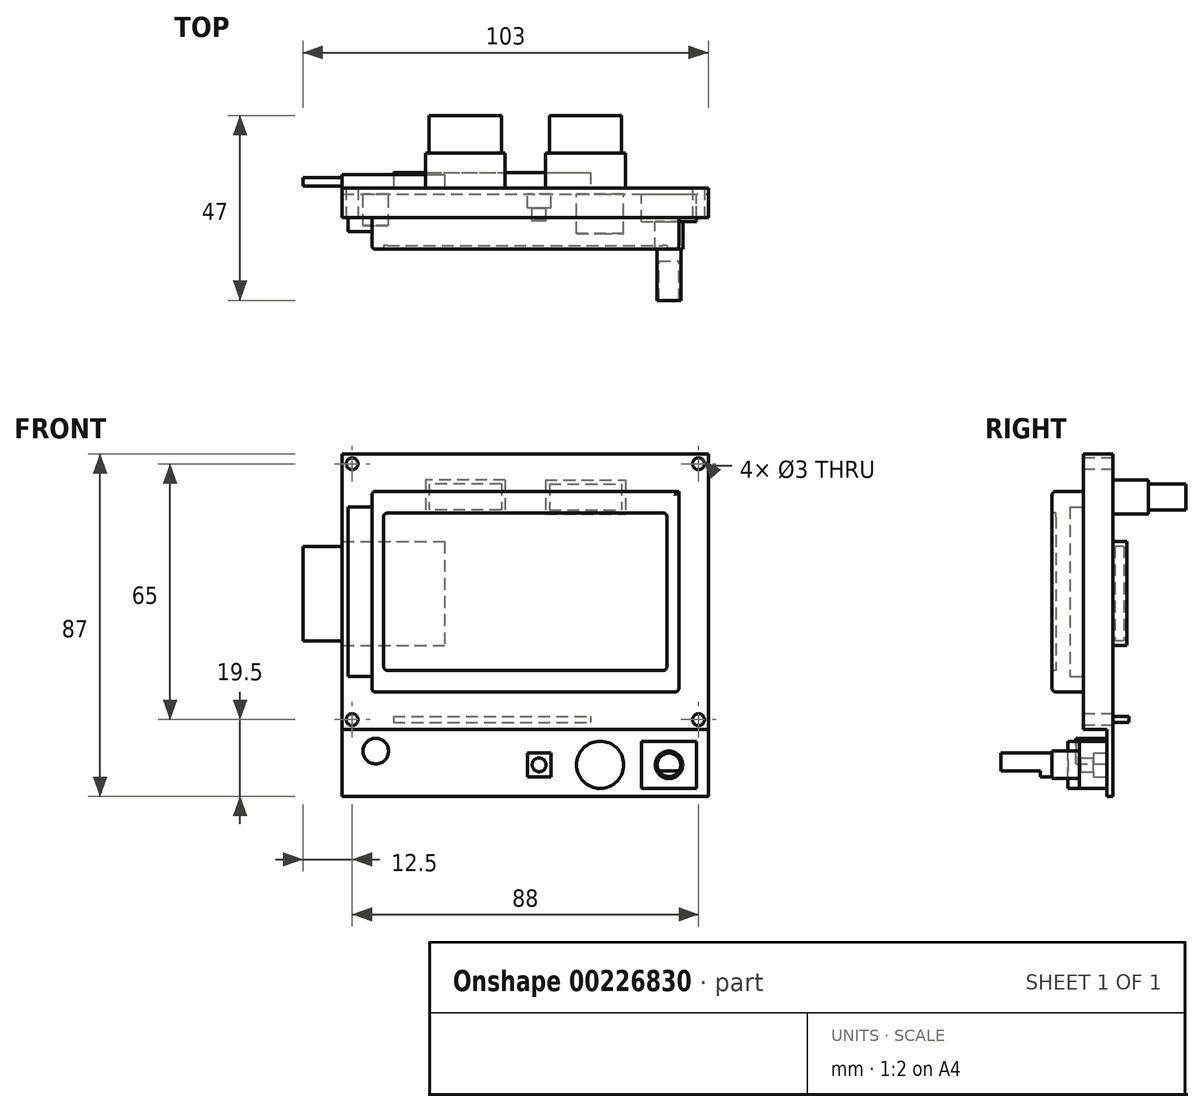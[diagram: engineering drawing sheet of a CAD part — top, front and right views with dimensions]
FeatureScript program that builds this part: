
annotation { "Feature Type Name" : "Feature", "Feature Type Description" : "" }
export const myFeature = defineFeature(function(context is Context, id is Id, definition is map)
    precondition{}
    {
        {
            var Q0;
            Q0=qCreatedBy(makeId("Front.planeOp"),FACE);
            var sketch = newSketch(context, id + "F0", { "sketchPlane" : qUnion([Q0])});
            skLineSegment(sketch, "E0.bottom", {"start": v(0, 0) * mm, "end": v(93, 0) * mm});
            skLineSegment(sketch, "E0.top", {"start": v(0, 87) * mm, "end": v(93, 87) * mm});
            skLineSegment(sketch, "E0.left", {"start": v(0, 0) * mm, "end": v(0, 87) * mm});
            skLineSegment(sketch, "E0.right", {"start": v(93, 0) * mm, "end": v(93, 87) * mm});
            skLineSegment(sketch, "E1", {"start": v(0, 17) * mm, "end": v(93, 17) * mm});
            skLineSegment(sketch, "E2.bottom", {"start": v(2.5, 84.5) * mm, "end": v(90.5, 84.5) * mm, "construction": true});
            skLineSegment(sketch, "E2.top", {"start": v(2.5, 19.5) * mm, "end": v(90.5, 19.5) * mm, "construction": true});
            skLineSegment(sketch, "E2.left", {"start": v(2.5, 84.5) * mm, "end": v(2.5, 19.5) * mm, "construction": true});
            skLineSegment(sketch, "E2.right", {"start": v(90.5, 84.5) * mm, "end": v(90.5, 19.5) * mm, "construction": true});
            skCircle(sketch, "E3", {"center": v(2.5, 84.5) * mm, "radius": 1.5 * mm});
            skCircle(sketch, "E4", {"center": v(90.5, 84.5) * mm, "radius": 1.5 * mm});
            skCircle(sketch, "E5", {"center": v(2.5, 19.5) * mm, "radius": 1.5 * mm});
            skCircle(sketch, "E6", {"center": v(90.5, 19.5) * mm, "radius": 1.5 * mm});
            skLineSegment(sketch, "E7", {"start": v(0, 8) * mm, "end": v(93, 8) * mm, "construction": true});
            skLineSegment(sketch, "E8", {"start": v(83, 11.72) * mm, "end": v(83, 4.4) * mm, "construction": true});
            skLineSegment(sketch, "E9.bottom", {"start": v(76, 2) * mm, "end": v(90, 2) * mm});
            skLineSegment(sketch, "E9.top", {"start": v(76, 14) * mm, "end": v(90, 14) * mm});
            skLineSegment(sketch, "E9.left", {"start": v(76, 2) * mm, "end": v(76, 14) * mm});
            skLineSegment(sketch, "E9.right", {"start": v(90, 2) * mm, "end": v(90, 14) * mm});
            skPoint(sketch, "E9.middle", {"position": v(83, 8) * mm});
            skCircle(sketch, "E10", {"center": v(83, 8) * mm, "radius": 3.5 * mm});
            skCircle(sketch, "E11", {"center": v(83, 8) * mm, "radius": 3 * mm});
            skLineSegment(sketch, "E12", {"start": v(80.4, 6.5) * mm, "end": v(85.6, 6.5) * mm});
            skCircle(sketch, "E13", {"center": v(65.5, 8) * mm, "radius": 6 * mm});
            skLineSegment(sketch, "E14.bottom", {"start": v(53, 11) * mm, "end": v(47, 11) * mm});
            skLineSegment(sketch, "E14.top", {"start": v(53, 5) * mm, "end": v(47, 5) * mm});
            skLineSegment(sketch, "E14.left", {"start": v(53, 11) * mm, "end": v(53, 5) * mm});
            skLineSegment(sketch, "E14.right", {"start": v(47, 11) * mm, "end": v(47, 5) * mm});
            skPoint(sketch, "E14.middle", {"position": v(50, 8) * mm});
            skCircle(sketch, "E15", {"center": v(50, 8) * mm, "radius": 1.75 * mm});
            skLineSegment(sketch, "E16", {"start": v(0, 11.5) * mm, "end": v(18.58, 11.5) * mm, "construction": true});
            skLineSegment(sketch, "E17", {"start": v(8.5, 14.77) * mm, "end": v(8.5, 6) * mm, "construction": true});
            skCircle(sketch, "E18", {"center": v(8.5, 11.5) * mm, "radius": 3.25 * mm});
            skSolve(sketch);
        }
        {
            var Q0;
            {var subQ2=sQuery(id+"F0.wireOp",EDGE,"E0.top");Q0=makeQuery(id+"F0.imprint","IMPRINT",FACE,{"disambiguationData":[TD([[makeQuery(id+"F0.imprint","IMPRINT",EDGE,{"derivedFrom":subQ2}),-1.0]])]});}
            var Q1;
            {var subQ0=sQuery(id+"F0.wireOp",EDGE,"E0.bottom");Q1=makeQuery(id+"F0.imprint","IMPRINT",FACE,{"disambiguationData":[TD([[makeQuery(id+"F0.imprint","IMPRINT",EDGE,{"derivedFrom":subQ0}),1.0]])]});}
            var Q2;
            Q2=makeQuery(id+"F0.imprint","IMPRINT",FACE,{"disambiguationData":[TD([[makeQuery(id+"F0.imprint","IMPRINT",EDGE,{"derivedFrom":sQuery(id+"F0.wireOp",EDGE,"E9.bottom")}),1.0]])]});
            var Q3;
            {var subQ0=sQuery(id+"F0.wireOp",EDGE,"E12");Q3=makeQuery(id+"F0.imprint","IMPRINT",FACE,{"disambiguationData":[TD([[makeQuery(id+"F0.imprint","IMPRINT",EDGE,{"derivedFrom":subQ0}),-1.0]])]});}
            var Q4;
            {var subQ0=sQuery(id+"F0.wireOp",EDGE,"E12");Q4=makeQuery(id+"F0.imprint","IMPRINT",FACE,{"disambiguationData":[TD([[makeQuery(id+"F0.imprint","IMPRINT",EDGE,{"derivedFrom":subQ0}),1.0]])]});}
            var Q5;
            Q5=makeQuery(id+"F0.imprint","IMPRINT",FACE,{"disambiguationData":[TD([[makeQuery(id+"F0.imprint","IMPRINT",EDGE,{"derivedFrom":sQuery(id+"F0.wireOp",EDGE,"E10")}),1.0]])]});
            var Q6;
            Q6=makeQuery(id+"F0.imprint","IMPRINT",FACE,{"disambiguationData":[TD([[makeQuery(id+"F0.imprint","IMPRINT",EDGE,{"derivedFrom":sQuery(id+"F0.wireOp",EDGE,"E14.bottom")}),1.0]])]});
            var Q7;
            Q7=makeQuery(id+"F0.imprint","IMPRINT",FACE,{"disambiguationData":[TD([[makeQuery(id+"F0.imprint","IMPRINT",EDGE,{"derivedFrom":sQuery(id+"F0.wireOp",EDGE,"E15")}),1.0]])]});
            var Q8;
            Q8=makeQuery(id+"F0.imprint","IMPRINT",FACE,{"disambiguationData":[TD([[makeQuery(id+"F0.imprint","IMPRINT",EDGE,{"derivedFrom":sQuery(id+"F0.wireOp",EDGE,"E13")}),1.0]])]});
            var Q9;
            Q9=makeQuery(id+"F0.imprint","IMPRINT",FACE,{"disambiguationData":[TD([[makeQuery(id+"F0.imprint","IMPRINT",EDGE,{"derivedFrom":sQuery(id+"F0.wireOp",EDGE,"E18")}),1.0]])]});
            extrude(context, id + "F1", {"entities" : qUnion([Q0, Q1, Q2, Q3, Q4, Q5, Q6, Q7, Q8, Q9]), "oppositeDirection" : true, "depth" : 1.5 * mm});
        }
        {
            var Q0;
            Q0=makeQuery(id+"F1.opExtrude","CAP_FACE",FACE,{"disambiguationData":[OSD([sQuery(id+"F0.wireOp",EDGE,"E0.bottom"),sQuery(id+"F0.wireOp",EDGE,"E0.top"),sQuery(id+"F0.wireOp",EDGE,"E0.left"),sQuery(id+"F0.wireOp",EDGE,"E0.right"),sQuery(id+"F0.wireOp",EDGE,"E3"),sQuery(id+"F0.wireOp",EDGE,"E4"),sQuery(id+"F0.wireOp",EDGE,"E5"),sQuery(id+"F0.wireOp",EDGE,"E6")])],"isStart":false});
            var sketch = newSketch(context, id + "F2", { "sketchPlane" : qUnion([Q0])});
            skLineSegment(sketch, "E19.bottom", {"start": v(-41.4, 80.4) * mm, "end": v(-21.1, 80.4) * mm});
            skLineSegment(sketch, "E19.top", {"start": v(-41.4, 71.7) * mm, "end": v(-21.1, 71.7) * mm});
            skLineSegment(sketch, "E19.left", {"start": v(-41.4, 80.4) * mm, "end": v(-41.4, 71.7) * mm});
            skLineSegment(sketch, "E19.right", {"start": v(-21.1, 80.4) * mm, "end": v(-21.1, 71.7) * mm});
            skLineSegment(sketch, "E20.bottom", {"start": v(-51.6, 80.4) * mm, "end": v(-71.9, 80.4) * mm});
            skLineSegment(sketch, "E20.top", {"start": v(-51.6, 71.7) * mm, "end": v(-71.9, 71.7) * mm});
            skLineSegment(sketch, "E20.left", {"start": v(-51.6, 80.4) * mm, "end": v(-51.6, 71.7) * mm});
            skLineSegment(sketch, "E20.right", {"start": v(-71.9, 80.4) * mm, "end": v(-71.9, 71.7) * mm});
            skLineSegment(sketch, "E21.0", {"start": v(-52.6, 79.4) * mm, "end": v(-70.9, 79.4) * mm});
            skLineSegment(sketch, "E21.1", {"start": v(-52.6, 79.4) * mm, "end": v(-52.6, 72.7) * mm});
            skLineSegment(sketch, "E21.2", {"start": v(-52.6, 72.7) * mm, "end": v(-70.9, 72.7) * mm});
            skLineSegment(sketch, "E21.3", {"start": v(-70.9, 79.4) * mm, "end": v(-70.9, 72.7) * mm});
            skLineSegment(sketch, "E22.0", {"start": v(-40.4, 79.4) * mm, "end": v(-22.1, 79.4) * mm});
            skLineSegment(sketch, "E22.1", {"start": v(-40.4, 79.4) * mm, "end": v(-40.4, 72.7) * mm});
            skLineSegment(sketch, "E22.2", {"start": v(-40.4, 72.7) * mm, "end": v(-22.1, 72.7) * mm});
            skLineSegment(sketch, "E22.3", {"start": v(-22.1, 79.4) * mm, "end": v(-22.1, 72.7) * mm});
            skLineSegment(sketch, "E23.bottom", {"start": v(0, 64.7) * mm, "end": v(-26, 64.7) * mm});
            skLineSegment(sketch, "E23.top", {"start": v(0, 38.35) * mm, "end": v(-26, 38.35) * mm});
            skLineSegment(sketch, "E23.left", {"start": v(0, 64.7) * mm, "end": v(0, 38.35) * mm});
            skLineSegment(sketch, "E23.right", {"start": v(-26, 64.7) * mm, "end": v(-26, 38.35) * mm});
            skLineSegment(sketch, "E24", {"start": v(-90.5, 19.5) * mm, "end": v(-2.5, 19.5) * mm, "construction": true});
            skLineSegment(sketch, "E25.bottom", {"start": v(-13, 20.25) * mm, "end": v(-63, 20.25) * mm});
            skLineSegment(sketch, "E25.top", {"start": v(-13, 18.75) * mm, "end": v(-63, 18.75) * mm});
            skLineSegment(sketch, "E25.left", {"start": v(-13, 20.25) * mm, "end": v(-13, 18.75) * mm});
            skLineSegment(sketch, "E25.right", {"start": v(-63, 20.25) * mm, "end": v(-63, 18.75) * mm});
            skPoint(sketch, "E25.middle", {"position": v(-38, 19.5) * mm});
            skSolve(sketch);
        }
        {
            var Q0;
            Q0=makeQuery(id+"F2.imprint","IMPRINT",FACE,{"disambiguationData":[TD([[makeQuery(id+"F2.imprint","IMPRINT",EDGE,{"derivedFrom":sQuery(id+"F2.wireOp",EDGE,"E20.bottom")}),1.0]])]});
            var Q1;
            Q1=makeQuery(id+"F2.imprint","IMPRINT",FACE,{"disambiguationData":[TD([[makeQuery(id+"F2.imprint","IMPRINT",EDGE,{"derivedFrom":sQuery(id+"F2.wireOp",EDGE,"E19.bottom")}),-1.0]])]});
            extrude(context, id + "F3", {"entities" : qUnion([Q0, Q1]), "operationType" : NewBodyOperationType.ADD, "depth" : 9 * mm});
        }
        {
            var Q0;
            Q0=makeQuery(id+"F2.imprint","IMPRINT",FACE,{"disambiguationData":[TD([[makeQuery(id+"F2.imprint","IMPRINT",EDGE,{"derivedFrom":sQuery(id+"F2.wireOp",EDGE,"E23.bottom")}),1.0]])]});
            extrude(context, id + "F4", {"entities" : qUnion([Q0]), "operationType" : NewBodyOperationType.ADD, "depth" : (5 - 1.5) * mm});
        }
        {
            var Q0;
            Q0=makeQuery(id+"F3.boolean.opBoolean","SPLIT",FACE,{"disambiguationData":[TD([makeQuery(id+"F3.opExtrude","SWEPT_FACE",FACE,{"disambiguationData":[OSD([sQuery(id+"F2.wireOp",EDGE,"E21.0")])]})])],"derivedFrom":makeQuery(id+"F1.opExtrude","CAP_FACE",FACE,{"disambiguationData":[OSD([sQuery(id+"F0.wireOp",EDGE,"E0.bottom"),sQuery(id+"F0.wireOp",EDGE,"E0.top"),sQuery(id+"F0.wireOp",EDGE,"E0.left"),sQuery(id+"F0.wireOp",EDGE,"E0.right"),sQuery(id+"F0.wireOp",EDGE,"E3"),sQuery(id+"F0.wireOp",EDGE,"E4"),sQuery(id+"F0.wireOp",EDGE,"E5"),sQuery(id+"F0.wireOp",EDGE,"E6")])],"isStart":false})});
            var Q1;
            Q1=makeQuery(id+"F3.boolean.opBoolean","SPLIT",FACE,{"disambiguationData":[TD([makeQuery(id+"F3.opExtrude","SWEPT_FACE",FACE,{"disambiguationData":[OSD([sQuery(id+"F2.wireOp",EDGE,"E22.0")])]})])],"derivedFrom":makeQuery(id+"F1.opExtrude","CAP_FACE",FACE,{"disambiguationData":[OSD([sQuery(id+"F0.wireOp",EDGE,"E0.bottom"),sQuery(id+"F0.wireOp",EDGE,"E0.top"),sQuery(id+"F0.wireOp",EDGE,"E0.left"),sQuery(id+"F0.wireOp",EDGE,"E0.right"),sQuery(id+"F0.wireOp",EDGE,"E3"),sQuery(id+"F0.wireOp",EDGE,"E4"),sQuery(id+"F0.wireOp",EDGE,"E5"),sQuery(id+"F0.wireOp",EDGE,"E6")])],"isStart":false})});
            extrude(context, id + "F5", {"entities" : qUnion([Q0, Q1]), "operationType" : NewBodyOperationType.ADD, "depth" : 18.5 * mm});
        }
        {
            var Q0;
            {var subQ2=sQuery(id+"F0.wireOp",EDGE,"E0.top");Q0=makeQuery(id+"F0.imprint","IMPRINT",FACE,{"disambiguationData":[TD([[makeQuery(id+"F0.imprint","IMPRINT",EDGE,{"derivedFrom":subQ2}),-1.0]])]});}
            extrude(context, id + "F6", {"entities" : qUnion([Q0]), "operationType" : NewBodyOperationType.ADD, "depth" : 6 * mm});
        }
        {
            var Q0;
            Q0=makeQuery(id+"F2.imprint","IMPRINT",FACE,{"disambiguationData":[TD([[makeQuery(id+"F2.imprint","IMPRINT",EDGE,{"derivedFrom":sQuery(id+"F2.wireOp",EDGE,"E25.bottom")}),1.0]])]});
            extrude(context, id + "F7", {"entities" : qUnion([Q0]), "operationType" : NewBodyOperationType.ADD, "depth" : 4 * mm});
        }
        {
            var Q0;
            Q0=makeQuery(id+"F0.imprint","IMPRINT",FACE,{"disambiguationData":[TD([[makeQuery(id+"F0.imprint","IMPRINT",EDGE,{"derivedFrom":sQuery(id+"F0.wireOp",EDGE,"E13")}),1.0]])]});
            extrude(context, id + "F8", {"entities" : qUnion([Q0]), "operationType" : NewBodyOperationType.ADD, "depth" : 10 * mm});
        }
        {
            var Q0;
            Q0=makeQuery(id+"F0.imprint","IMPRINT",FACE,{"disambiguationData":[TD([[makeQuery(id+"F0.imprint","IMPRINT",EDGE,{"derivedFrom":sQuery(id+"F0.wireOp",EDGE,"E14.bottom")}),1.0]])]});
            extrude(context, id + "F9", {"entities" : qUnion([Q0]), "operationType" : NewBodyOperationType.ADD, "depth" : (5 - 1.5) * mm});
        }
        {
            var Q0;
            Q0=makeQuery(id+"F0.imprint","IMPRINT",FACE,{"disambiguationData":[TD([[makeQuery(id+"F0.imprint","IMPRINT",EDGE,{"derivedFrom":sQuery(id+"F0.wireOp",EDGE,"E15")}),1.0]])]});
            extrude(context, id + "F10", {"entities" : qUnion([Q0]), "operationType" : NewBodyOperationType.ADD, "depth" : 6.7 * mm});
        }
        {
            var Q0;
            {var subQ0=sQuery(id+"F0.wireOp",EDGE,"E12");Q0=makeQuery(id+"F0.imprint","IMPRINT",FACE,{"disambiguationData":[TD([[makeQuery(id+"F0.imprint","IMPRINT",EDGE,{"derivedFrom":subQ0}),1.0]])]});}
            extrude(context, id + "F11", {"entities" : qUnion([Q0]), "operationType" : NewBodyOperationType.ADD, "depth" : 27 * mm});
        }
        {
            var Q0;
            {var subQ0=sQuery(id+"F0.wireOp",EDGE,"E12");Q0=makeQuery(id+"F0.imprint","IMPRINT",FACE,{"disambiguationData":[TD([[makeQuery(id+"F0.imprint","IMPRINT",EDGE,{"derivedFrom":subQ0}),-1.0]])]});}
            extrude(context, id + "F12", {"entities" : qUnion([Q0]), "operationType" : NewBodyOperationType.ADD, "depth" : 17 * mm});
        }
        {
            var Q0;
            Q0=makeQuery(id+"F0.imprint","IMPRINT",FACE,{"disambiguationData":[TD([[makeQuery(id+"F0.imprint","IMPRINT",EDGE,{"derivedFrom":sQuery(id+"F0.wireOp",EDGE,"E10")}),1.0]])]});
            var Q1;
            {var subQ0=sQuery(id+"F0.wireOp",EDGE,"E12");Q1=makeQuery(id+"F0.imprint","IMPRINT",FACE,{"disambiguationData":[TD([[makeQuery(id+"F0.imprint","IMPRINT",EDGE,{"derivedFrom":subQ0}),-1.0]])]});}
            var Q2;
            {var subQ0=sQuery(id+"F0.wireOp",EDGE,"E12");Q2=makeQuery(id+"F0.imprint","IMPRINT",FACE,{"disambiguationData":[TD([[makeQuery(id+"F0.imprint","IMPRINT",EDGE,{"derivedFrom":subQ0}),1.0]])]});}
            extrude(context, id + "F13", {"entities" : qUnion([Q0, Q1, Q2]), "operationType" : NewBodyOperationType.ADD, "depth" : 14 * mm});
        }
        {
            var Q0;
            Q0=makeQuery(id+"F0.imprint","IMPRINT",FACE,{"disambiguationData":[TD([[makeQuery(id+"F0.imprint","IMPRINT",EDGE,{"derivedFrom":sQuery(id+"F0.wireOp",EDGE,"E9.bottom")}),1.0]])]});
            extrude(context, id + "F14", {"entities" : qUnion([Q0]), "operationType" : NewBodyOperationType.ADD, "depth" : 7 * mm});
        }
        {
            var Q0;
            Q0=makeQuery(id+"F0.imprint","IMPRINT",FACE,{"disambiguationData":[TD([[makeQuery(id+"F0.imprint","IMPRINT",EDGE,{"derivedFrom":sQuery(id+"F0.wireOp",EDGE,"E18")}),1.0]])]});
            extrude(context, id + "F15", {"entities" : qUnion([Q0]), "operationType" : NewBodyOperationType.ADD, "depth" : 8 * mm});
        }
        {
            var Q0;
            Q0=makeQuery(id+"F6.opExtrude","CAP_FACE",FACE,{"disambiguationData":[OSD([sQuery(id+"F0.wireOp",EDGE,"E0.top"),sQuery(id+"F0.wireOp",EDGE,"E0.left"),sQuery(id+"F0.wireOp",EDGE,"E0.right"),sQuery(id+"F0.wireOp",EDGE,"E1"),sQuery(id+"F0.wireOp",EDGE,"E3"),sQuery(id+"F0.wireOp",EDGE,"E4"),sQuery(id+"F0.wireOp",EDGE,"E5"),sQuery(id+"F0.wireOp",EDGE,"E6")])],"isStart":false});
            var sketch = newSketch(context, id + "F16", { "sketchPlane" : qUnion([Q0])});
            skLineSegment(sketch, "E26.bottom", {"start": v(7.5, 77.5) * mm, "end": v(85.5, 77.5) * mm});
            skLineSegment(sketch, "E26.top", {"start": v(7.5, 26.5) * mm, "end": v(85.5, 26.5) * mm});
            skLineSegment(sketch, "E26.left", {"start": v(7.5, 77.5) * mm, "end": v(7.5, 26.5) * mm});
            skLineSegment(sketch, "E26.right", {"start": v(85.5, 77.5) * mm, "end": v(85.5, 26.5) * mm});
            skLineSegment(sketch, "E27.bottom", {"start": v(1.5, 73.5) * mm, "end": v(7.5, 73.5) * mm});
            skLineSegment(sketch, "E27.top", {"start": v(1.5, 30.5) * mm, "end": v(7.5, 30.5) * mm});
            skLineSegment(sketch, "E27.left", {"start": v(1.5, 73.5) * mm, "end": v(1.5, 30.5) * mm});
            skLineSegment(sketch, "E27.right", {"start": v(7.5, 73.5) * mm, "end": v(7.5, 30.5) * mm});
            skSolve(sketch);
        }
        {
            var Q0;
            Q0=makeQuery(id+"F16.imprint","IMPRINT",FACE,{"disambiguationData":[TD([[makeQuery(id+"F16.imprint","IMPRINT",EDGE,{"derivedFrom":sQuery(id+"F16.wireOp",EDGE,"E27.bottom")}),-1.0]])]});
            extrude(context, id + "F17", {"entities" : qUnion([Q0]), "operationType" : NewBodyOperationType.ADD, "depth" : 3.5 * mm});
        }
        {
            var Q0;
            {var subQ3=sQuery(id+"F16.wireOp",EDGE,"E26.bottom");Q0=makeQuery(id+"F16.imprint","IMPRINT",FACE,{"disambiguationData":[TD([[makeQuery(id+"F16.imprint","IMPRINT",EDGE,{"derivedFrom":subQ3}),-1.0]])]});}
            extrude(context, id + "F18", {"entities" : qUnion([Q0]), "operationType" : NewBodyOperationType.ADD, "depth" : 8 * mm});
        }
        {
            var Q0;
            Q0=makeQuery(id+"F18.opExtrude","CAP_EDGE",EDGE,{"disambiguationData":[OSD([sQuery(id+"F16.wireOp",EDGE,"E26.left"),sQuery(id+"F16.wireOp",EDGE,"E27.right")])],"isStart":false});
            var Q1;
            Q1=makeQuery(id+"F18.opExtrude","CAP_EDGE",EDGE,{"disambiguationData":[OSD([sQuery(id+"F16.wireOp",EDGE,"E26.bottom")])],"isStart":false});
            var Q2;
            Q2=makeQuery(id+"F18.opExtrude","CAP_EDGE",EDGE,{"disambiguationData":[OSD([sQuery(id+"F16.wireOp",EDGE,"E26.top")])],"isStart":false});
            var Q3;
            Q3=makeQuery(id+"F18.opExtrude","CAP_EDGE",EDGE,{"disambiguationData":[OSD([sQuery(id+"F16.wireOp",EDGE,"E26.right")])],"isStart":false});
            var Q4;
            Q4=makeQuery(id+"F18.opExtrude","SWEPT_EDGE",EDGE,{"disambiguationData":[OSD([sQuery(id+"F16.wireOp",EDGE,"E26.top"),sQuery(id+"F16.wireOp",EDGE,"E26.left")])]});
            var Q5;
            Q5=makeQuery(id+"F18.opExtrude","SWEPT_EDGE",EDGE,{"disambiguationData":[OSD([sQuery(id+"F16.wireOp",EDGE,"E26.top"),sQuery(id+"F16.wireOp",EDGE,"E26.right")])]});
            var Q6;
            Q6=makeQuery(id+"F18.opExtrude","SWEPT_EDGE",EDGE,{"disambiguationData":[OSD([sQuery(id+"F16.wireOp",EDGE,"E26.bottom"),sQuery(id+"F16.wireOp",EDGE,"E26.left")])]});
            fillet(context, id + "F19", {"entities" : qUnion([Q0, Q1, Q2, Q3, Q4, Q5, Q6]), "radius" : 1 * mm, "tangentPropagation" : true, "allowEdgeOverflow" : false});
        }
        {
            var Q0;
            Q0=makeQuery(id+"F18.opExtrude","CAP_FACE",FACE,{"disambiguationData":[OSD([sQuery(id+"F16.wireOp",EDGE,"E26.bottom"),sQuery(id+"F16.wireOp",EDGE,"E26.top"),sQuery(id+"F16.wireOp",EDGE,"E26.left"),sQuery(id+"F16.wireOp",EDGE,"E26.right"),sQuery(id+"F16.wireOp",EDGE,"E27.right")])],"isStart":false});
            var sketch = newSketch(context, id + "F20", { "sketchPlane" : qUnion([Q0])});
            skLineSegment(sketch, "E28.bottom", {"start": v(11.5, 72) * mm, "end": v(81.5, 72) * mm});
            skLineSegment(sketch, "E28.top", {"start": v(11.5, 32) * mm, "end": v(81.5, 32) * mm});
            skLineSegment(sketch, "E28.left", {"start": v(10.5, 71) * mm, "end": v(10.5, 33) * mm});
            skLineSegment(sketch, "E28.right", {"start": v(82.5, 71) * mm, "end": v(82.5, 33) * mm});
            skPoint(sketch, "E28.middle", {"position": v(46.5, 52) * mm});
            skLineSegment(sketch, "E29", {"start": v(46.5, 52) * mm, "end": v(46.5, 76.5) * mm, "construction": true});
            skLineSegment(sketch, "E30", {"start": v(46.5, 52) * mm, "end": v(84.5, 52) * mm, "construction": true});
            skPoint(sketch, "E31.visualSharp", {"position": v(10.5, 72) * mm});
            skArc(sketch, "E31.filletArc", {"start": v(11.5, 72) * mm, "mid": v(10.8, 71.7) * mm, "end": v(10.5, 71) * mm});
            skPoint(sketch, "E32.visualSharp", {"position": v(82.5, 72) * mm});
            skArc(sketch, "E32.filletArc", {"start": v(82.5, 71) * mm, "mid": v(82.2, 71.7) * mm, "end": v(81.5, 72) * mm});
            skPoint(sketch, "E33.visualSharp", {"position": v(82.5, 32) * mm});
            skArc(sketch, "E33.filletArc", {"start": v(81.5, 32) * mm, "mid": v(82.2, 32.3) * mm, "end": v(82.5, 33) * mm});
            skPoint(sketch, "E34.visualSharp", {"position": v(10.5, 32) * mm});
            skArc(sketch, "E34.filletArc", {"start": v(10.5, 33) * mm, "mid": v(10.8, 32.3) * mm, "end": v(11.5, 32) * mm});
            skSolve(sketch);
        }
        {
            var Q0;
            Q0=makeQuery(id+"F20.imprint","IMPRINT",FACE,{"disambiguationData":[TD([[makeQuery(id+"F20.imprint","IMPRINT",EDGE,{"derivedFrom":sQuery(id+"F20.wireOp",EDGE,"E28.bottom")}),-1.0]])]});
            extrude(context, id + "F21", {"entities" : qUnion([Q0]), "operationType" : NewBodyOperationType.REMOVE, "oppositeDirection" : true, "depth" : 1 * mm});
        }
        {
            var Q0;
            {var subQ0=sQuery(id+"F0.wireOp",EDGE,"E0.left");Q0=makeQuery(id+"F6.boolean.opBoolean","MERGE",FACE,{"derivedFrom":[makeQuery(id+"F4.boolean.opBoolean","MERGE",FACE,{"derivedFrom":[makeQuery(id+"F1.opExtrude","SWEPT_FACE",FACE,{"disambiguationData":[OSD([subQ0])]}),makeQuery(id+"F4.opExtrude","SWEPT_FACE",FACE,{"disambiguationData":[OSD([sQuery(id+"F2.wireOp",EDGE,"E23.left")])]})]}),makeQuery(id+"F6.opExtrude","SWEPT_FACE",FACE,{"disambiguationData":[OSD([subQ0])]})]});}
            var sketch = newSketch(context, id + "F22", { "sketchPlane" : qUnion([Q0])});
            skLineSegment(sketch, "E35.bottom", {"start": v(-4.2, 63.53) * mm, "end": v(-2, 63.53) * mm});
            skLineSegment(sketch, "E35.top", {"start": v(-4.2, 39.53) * mm, "end": v(-2, 39.53) * mm});
            skLineSegment(sketch, "E35.left", {"start": v(-4.2, 63.53) * mm, "end": v(-4.2, 39.53) * mm});
            skLineSegment(sketch, "E35.right", {"start": v(-2, 63.53) * mm, "end": v(-2, 39.53) * mm});
            skLineSegment(sketch, "E36", {"start": v(-5, 51.53) * mm, "end": v(-4.2, 51.53) * mm, "construction": true});
            skSolve(sketch);
        }
        {
            var Q0;
            Q0=makeQuery(id+"F22.imprint","IMPRINT",FACE,{"disambiguationData":[TD([[makeQuery(id+"F22.imprint","IMPRINT",EDGE,{"derivedFrom":sQuery(id+"F22.wireOp",EDGE,"E35.bottom")}),-1.0]])]});
            extrude(context, id + "F23", {"entities" : qUnion([Q0]), "operationType" : NewBodyOperationType.ADD, "depth" : 10 * mm});
        }
    });
